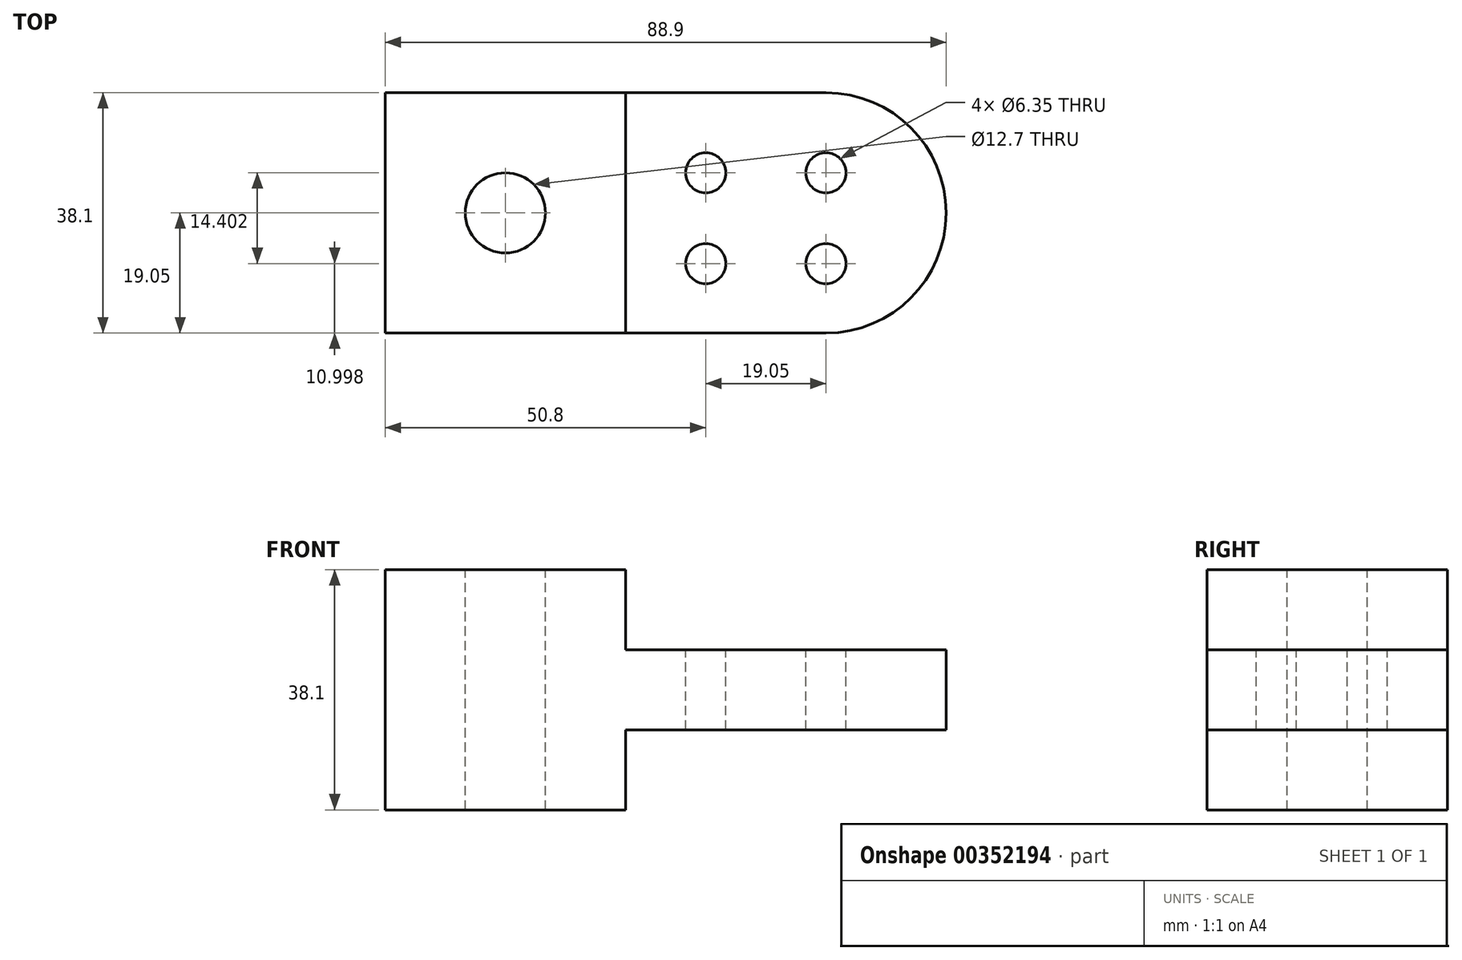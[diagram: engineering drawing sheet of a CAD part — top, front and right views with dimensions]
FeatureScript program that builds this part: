
annotation { "Feature Type Name" : "Feature", "Feature Type Description" : "" }
export const myFeature = defineFeature(function(context is Context, id is Id, definition is map)
    precondition{}
    {
        {
            var Q0;
            Q0=qCreatedBy(makeId("Front.planeOp"),FACE);
            var sketch = newSketch(context, id + "F0", { "sketchPlane" : qUnion([Q0])});
            skLineSegment(sketch, "E0", {"start": v(0, 0) * mm, "end": v(0, 38.1) * mm});
            skLineSegment(sketch, "E1", {"start": v(0, 38.1) * mm, "end": v(38.1, 38.1) * mm});
            skLineSegment(sketch, "E2", {"start": v(38.1, 38.1) * mm, "end": v(38.1, 25.4) * mm});
            skLineSegment(sketch, "E3", {"start": v(38.1, 25.4) * mm, "end": v(88.9, 25.4) * mm});
            skLineSegment(sketch, "E4", {"start": v(88.9, 25.4) * mm, "end": v(88.9, 12.7) * mm});
            skLineSegment(sketch, "E5", {"start": v(88.9, 12.7) * mm, "end": v(38.1, 12.7) * mm});
            skLineSegment(sketch, "E6", {"start": v(38.1, 12.7) * mm, "end": v(38.1, 0) * mm});
            skLineSegment(sketch, "E7", {"start": v(38.1, 0) * mm, "end": v(0, 0) * mm});
            skSolve(sketch);
        }
        {
            var Q0;
            Q0 = qSketchRegion(id + "F0", true);
            extrude(context, id + "F1", {"entities" : qUnion([Q0]), "depth" : 38.1 * mm});
        }
        {
            var Q0;
            Q0=makeQuery(id+"F1.opExtrude","SWEPT_FACE",FACE,{"disambiguationData":[OSD([sQuery(id+"F0.wireOp",EDGE,"E1")])]});
            var sketch = newSketch(context, id + "F2", { "sketchPlane" : qUnion([Q0])});
            skCircle(sketch, "E8", {"center": v(19.05, -19.05) * mm, "radius": 6.35 * mm});
            skCircle(sketch, "E9", {"center": v(50.8, -12.7) * mm, "radius": 3.18 * mm});
            skCircle(sketch, "E10", {"center": v(50.8, -27.1) * mm, "radius": 3.18 * mm});
            skCircle(sketch, "E11", {"center": v(69.85, -27.1) * mm, "radius": 3.18 * mm});
            skCircle(sketch, "E12", {"center": v(69.85, -12.7) * mm, "radius": 3.18 * mm});
            skSolve(sketch);
        }
        {
            var Q0;
            Q0 = qSketchRegion(id + "F2", true);
            extrude(context, id + "F3", {"entities" : qUnion([Q0]), "operationType" : NewBodyOperationType.REMOVE, "endBound" : BoundingType.THROUGH_ALL, "oppositeDirection" : true, "depth" : 25.4 * mm});
        }
        {
            var Q0;
            Q0=makeQuery(id+"F1.opExtrude","SWEPT_FACE",FACE,{"disambiguationData":[OSD([sQuery(id+"F0.wireOp",EDGE,"E3")])]});
            var sketch = newSketch(context, id + "F4", { "sketchPlane" : qUnion([Q0])});
            skLineSegment(sketch, "E13", {"start": v(38.1, 0) * mm, "end": v(38.1, -38.1) * mm});
            skLineSegment(sketch, "E14", {"start": v(38.1, -38.1) * mm, "end": v(69.85, -38.1) * mm});
            skLineSegment(sketch, "E15", {"start": v(38.1, 0) * mm, "end": v(69.85, 0) * mm});
            skArc(sketch, "E16", {"start": v(69.85, -38.1) * mm, "mid": v(88.9, -19.05) * mm, "end": v(69.85, 0) * mm});
            skSolve(sketch);
        }
        {
            var Q0;
            {var subQ0=sQuery(id+"F4.wireOp",EDGE,"E16");var subQ1=sQuery(id+"F0.wireOp",EDGE,"E3");var subQ2=makeQuery(id+"F1.opExtrude","CAP_EDGE",EDGE,{"disambiguationData":[OSD([subQ1])],"isStart":true});var subQ3=makeQuery(id+"F4.imprint","INTERSECT",VERTEX,{"derivedFrom":[subQ2,sQuery(id+"F4.wireOp",EDGE,"E15"),subQ0]});Q0=makeQuery(id+"F4.imprint","IMPRINT",FACE,{"disambiguationData":[TD([[makeQuery(id+"F4.imprint","IMPRINT",EDGE,{"disambiguationData":[TD([[subQ3,1.0]])],"derivedFrom":subQ0}),-1.0]])]});}
            var Q1;
            {var subQ0=sQuery(id+"F4.wireOp",EDGE,"E16");var subQ1=sQuery(id+"F0.wireOp",EDGE,"E3");var subQ2=makeQuery(id+"F1.opExtrude","CAP_EDGE",EDGE,{"disambiguationData":[OSD([subQ1])],"isStart":false});var subQ3=makeQuery(id+"F4.imprint","INTERSECT",VERTEX,{"derivedFrom":[subQ2,sQuery(id+"F4.wireOp",EDGE,"E14"),subQ0]});Q1=makeQuery(id+"F4.imprint","IMPRINT",FACE,{"disambiguationData":[TD([[makeQuery(id+"F4.imprint","IMPRINT",EDGE,{"disambiguationData":[TD([[subQ3,-1.0]])],"derivedFrom":subQ0}),-1.0]])]});}
            extrude(context, id + "F5", {"entities" : qUnion([Q0, Q1]), "operationType" : NewBodyOperationType.REMOVE, "endBound" : BoundingType.THROUGH_ALL, "oppositeDirection" : true, "depth" : 25.4 * mm});
        }
    });
